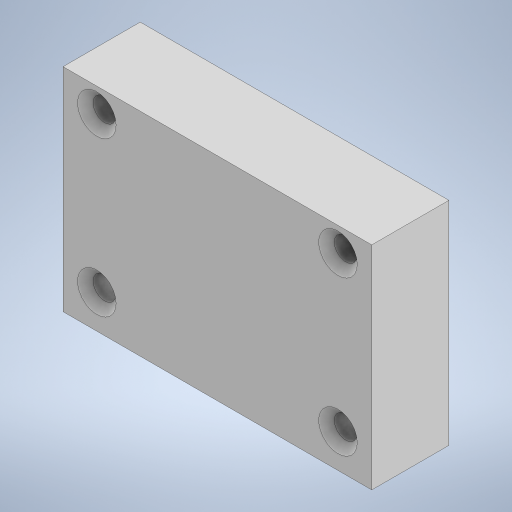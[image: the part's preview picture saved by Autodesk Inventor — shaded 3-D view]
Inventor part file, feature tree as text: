
AUTODESK INVENTOR PART (.ipt)
format: ipt  version: 2023 (Build 270158000, 158)  size: 270,336 bytes
history: native  units: mm
features: sketch x3, extrude x2, hole x1
ambient origin geometry x8: Origin, YZ Plane, XZ Plane, XY Plane, X Axis, Y Axis, Z Axis, Center Point
bodies: Solid1 (feature_tree)
feature tree (6):
  sketch  "Sketch1"  dims[d0=32.0mm d1=22.0mm]
  extrude  "Extrusion1"  Depth=22.0mm
  hole  "Hole1"  [1 undecoded]
  extrude  "Extrusion2"  Depth=8.0mm TaperAngle=0.0deg
  sketch  "Sketch3"  dims[d4=2.5mm d5=8.0mm d6=0.0mm d7=2.38125mm d8=6.0mm d9=4.0mm d10=2.0mm d11=90.0deg d12=10.0mm d13=20.594885mm d14=21.0mm d15=18.5mm d16=3.5mm d17=0.0mm]
  sketch  "Sketch2"  dims[d2=3.5mm d3=3.5mm]
note: 1 required parameter value undecoded (feature->parameter linkage not recoverable at this tier; creation-order binding heuristic only, values carry confidence <= 0.55)
